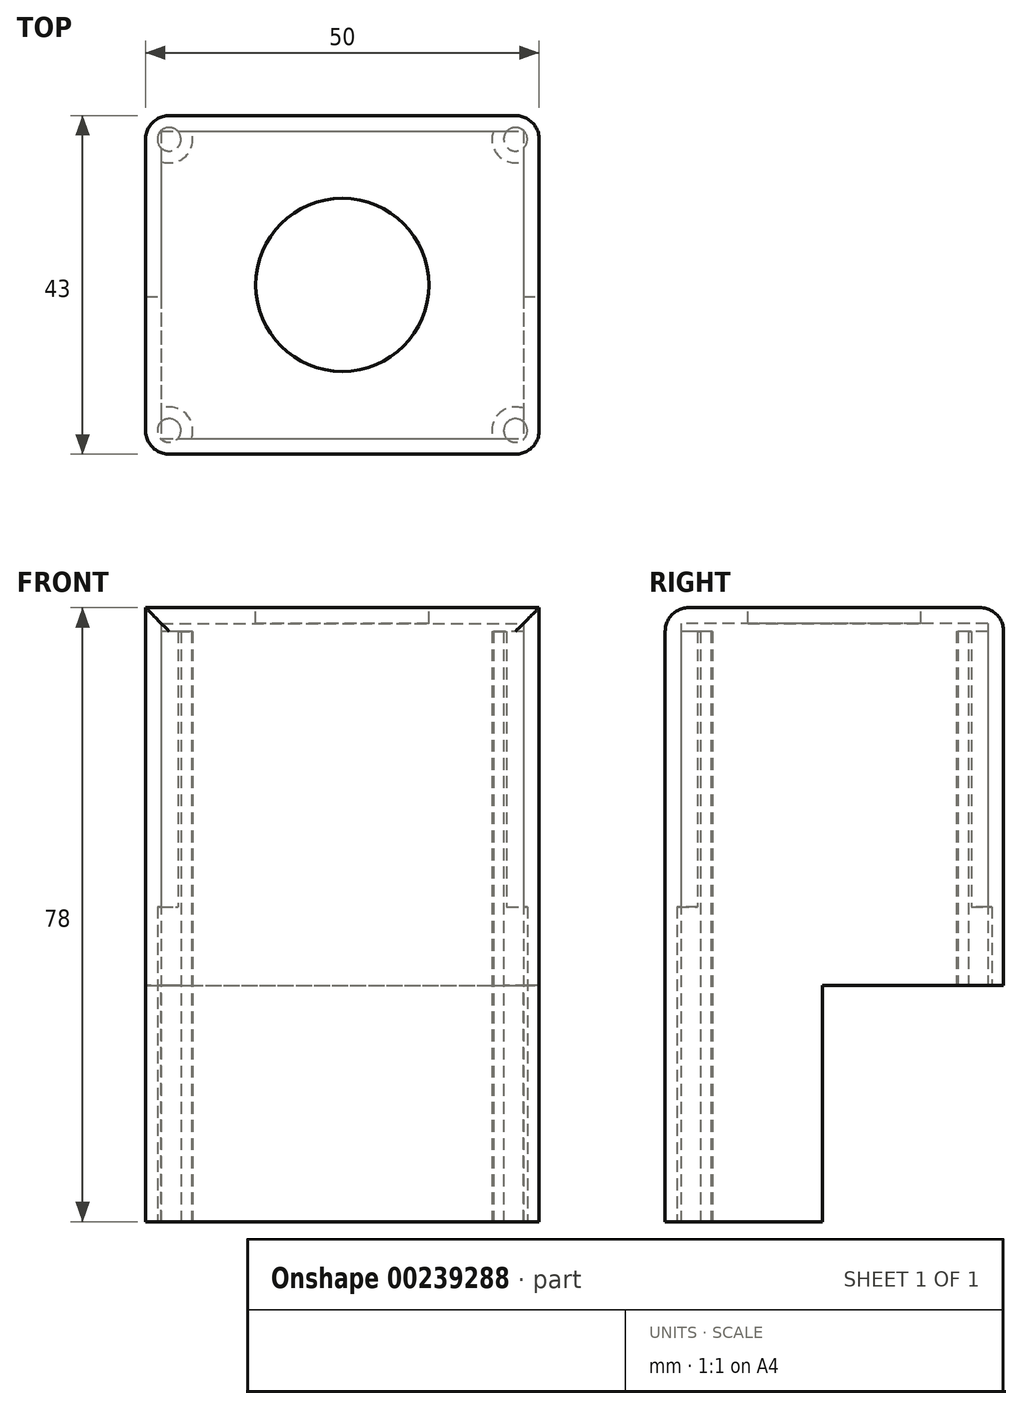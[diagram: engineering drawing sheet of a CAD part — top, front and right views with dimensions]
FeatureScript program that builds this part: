
annotation { "Feature Type Name" : "Feature", "Feature Type Description" : "" }
export const myFeature = defineFeature(function(context is Context, id is Id, definition is map)
    precondition{}
    {
        {
            var Q0;
            Q0=qCreatedBy(makeId("Top.planeOp"),FACE);
            var sketch = newSketch(context, id + "F0", { "sketchPlane" : qUnion([Q0])});
            skLineSegment(sketch, "E0.bottom", {"start": v(-34.03, 26.22) * mm, "end": v(15.97, 26.22) * mm});
            skLineSegment(sketch, "E0.top", {"start": v(-34.03, -16.78) * mm, "end": v(15.97, -16.78) * mm});
            skLineSegment(sketch, "E0.left", {"start": v(-34.03, 26.22) * mm, "end": v(-34.03, -16.78) * mm});
            skLineSegment(sketch, "E0.right", {"start": v(15.97, 26.22) * mm, "end": v(15.97, -16.78) * mm});
            skPoint(sketch, "E1", {"position": v(-31.03, -13.78) * mm});
            skPoint(sketch, "E2", {"position": v(-31.03, 23.22) * mm});
            skPoint(sketch, "E3", {"position": v(12.97, 23.22) * mm});
            skPoint(sketch, "E4", {"position": v(12.97, -13.78) * mm});
            skCircle(sketch, "E5", {"center": v(-31.03, 23.22) * mm, "radius": 1.5 * mm});
            skCircle(sketch, "E6", {"center": v(12.97, 23.22) * mm, "radius": 1.5 * mm});
            skCircle(sketch, "E7", {"center": v(-31.03, -13.78) * mm, "radius": 1.5 * mm});
            skCircle(sketch, "E8", {"center": v(12.97, -13.78) * mm, "radius": 1.5 * mm});
            skSolve(sketch);
        }
        {
            var Q0;
            Q0=makeQuery(id+"F0.imprint","IMPRINT",FACE,{"disambiguationData":[TD([[makeQuery(id+"F0.imprint","IMPRINT",EDGE,{"derivedFrom":sQuery(id+"F0.wireOp",EDGE,"E8")}),-1.0]])]});
            var Q1;
            Q1=makeQuery(id+"F0.imprint","IMPRINT",FACE,{"disambiguationData":[TD([[makeQuery(id+"F0.imprint","IMPRINT",EDGE,{"derivedFrom":sQuery(id+"F0.wireOp",EDGE,"E7")}),-1.0]])]});
            var Q2;
            Q2=makeQuery(id+"F0.imprint","IMPRINT",FACE,{"disambiguationData":[TD([[makeQuery(id+"F0.imprint","IMPRINT",EDGE,{"derivedFrom":sQuery(id+"F0.wireOp",EDGE,"E5")}),-1.0]])]});
            var Q3;
            Q3=makeQuery(id+"F0.imprint","IMPRINT",FACE,{"disambiguationData":[TD([[makeQuery(id+"F0.imprint","IMPRINT",EDGE,{"derivedFrom":sQuery(id+"F0.wireOp",EDGE,"E6")}),-1.0]])]});
            var Q4;
            {var subQ5=sQuery(id+"F0.wireOp",EDGE,"5a7f028d-dde4-426a-927e-fdb31705949f");var subQ13=sQuery(id+"F0.wireOp",EDGE,"E0.bottom");var subQ14=makeQuery(id+"F0.imprint","INTERSECT",VERTEX,{"derivedFrom":[subQ13,subQ5]});Q4=makeQuery(id+"F0.imprint","IMPRINT",FACE,{"disambiguationData":[TD([[makeQuery(id+"F0.imprint","IMPRINT",EDGE,{"disambiguationData":[TD([[subQ14,-1.0]])],"derivedFrom":subQ13}),-1.0]])]});}
            var Q5;
            Q5=makeQuery(id+"F0.imprint","IMPRINT",FACE,{"disambiguationData":[TD([[makeQuery(id+"F0.imprint","IMPRINT",EDGE,{"derivedFrom":sQuery(id+"F0.wireOp",EDGE,"E6")}),1.0]])]});
            var Q6;
            Q6=makeQuery(id+"F0.imprint","IMPRINT",FACE,{"disambiguationData":[TD([[makeQuery(id+"F0.imprint","IMPRINT",EDGE,{"derivedFrom":sQuery(id+"F0.wireOp",EDGE,"E8")}),1.0]])]});
            var Q7;
            Q7=makeQuery(id+"F0.imprint","IMPRINT",FACE,{"disambiguationData":[TD([[makeQuery(id+"F0.imprint","IMPRINT",EDGE,{"derivedFrom":sQuery(id+"F0.wireOp",EDGE,"E7")}),1.0]])]});
            var Q8;
            Q8=makeQuery(id+"F0.imprint","IMPRINT",FACE,{"disambiguationData":[TD([[makeQuery(id+"F0.imprint","IMPRINT",EDGE,{"derivedFrom":sQuery(id+"F0.wireOp",EDGE,"E5")}),1.0]])]});
            extrude(context, id + "F1", {"entities" : qUnion([Q0, Q1, Q2, Q3, Q4, Q5, Q6, Q7, Q8]), "depth" : 78 * mm});
        }
        {
            var Q0;
            Q0=makeQuery(id+"F1.opExtrude","CAP_FACE",FACE,{"disambiguationData":[OSD([sQuery(id+"F0.wireOp",EDGE,"E0.bottom"),sQuery(id+"F0.wireOp",EDGE,"E0.top"),sQuery(id+"F0.wireOp",EDGE,"E0.left"),sQuery(id+"F0.wireOp",EDGE,"E0.right")])],"isStart":false});
            var sketch = newSketch(context, id + "F2", { "sketchPlane" : qUnion([Q0])});
            skCircle(sketch, "E9", {"center": v(-9.03, 4.72) * mm, "radius": 11 * mm});
            skSolve(sketch);
        }
        {
            var Q0;
            Q0=makeQuery(id+"F1.opExtrude","CAP_FACE",FACE,{"disambiguationData":[OSD([sQuery(id+"F0.wireOp",EDGE,"E0.bottom"),sQuery(id+"F0.wireOp",EDGE,"E0.top"),sQuery(id+"F0.wireOp",EDGE,"E0.left"),sQuery(id+"F0.wireOp",EDGE,"E0.right")])],"isStart":true});
            shell(context, id + "F3", {"entities" : qUnion([Q0]), "thickness" : 2 * mm});
        }
        {
            var Q0;
            Q0=makeQuery(id+"F2.imprint","IMPRINT",FACE,{"disambiguationData":[TD([[makeQuery(id+"F2.imprint","IMPRINT",EDGE,{"derivedFrom":sQuery(id+"F2.wireOp",EDGE,"E9")}),1.0]])]});
            extrude(context, id + "F4", {"entities" : qUnion([Q0]), "operationType" : NewBodyOperationType.REMOVE, "oppositeDirection" : true, "depth" : 3.1 * mm});
        }
        {
            var Q0;
            Q0=makeQuery(id+"F1.opExtrude","SWEPT_EDGE",EDGE,{"disambiguationData":[OSD([sQuery(id+"F0.wireOp",EDGE,"E0.bottom"),sQuery(id+"F0.wireOp",EDGE,"E0.right")])]});
            var Q1;
            Q1=makeQuery(id+"F1.opExtrude","CAP_EDGE",EDGE,{"disambiguationData":[OSD([sQuery(id+"F0.wireOp",EDGE,"E0.bottom")])],"isStart":false});
            var Q2;
            Q2=makeQuery(id+"F1.opExtrude","SWEPT_EDGE",EDGE,{"disambiguationData":[OSD([sQuery(id+"F0.wireOp",EDGE,"E0.bottom"),sQuery(id+"F0.wireOp",EDGE,"E0.left")])]});
            var Q3;
            Q3=makeQuery(id+"F1.opExtrude","SWEPT_EDGE",EDGE,{"disambiguationData":[OSD([sQuery(id+"F0.wireOp",EDGE,"E0.top"),sQuery(id+"F0.wireOp",EDGE,"E0.right")])]});
            var Q4;
            Q4=makeQuery(id+"F1.opExtrude","CAP_EDGE",EDGE,{"disambiguationData":[OSD([sQuery(id+"F0.wireOp",EDGE,"E0.top")])],"isStart":false});
            var Q5;
            Q5=makeQuery(id+"F1.opExtrude","SWEPT_EDGE",EDGE,{"disambiguationData":[OSD([sQuery(id+"F0.wireOp",EDGE,"E0.top"),sQuery(id+"F0.wireOp",EDGE,"E0.left")])]});
            fillet(context, id + "F5", {"entities" : qUnion([Q0, Q1, Q2, Q3, Q4, Q5]), "radius" : 3 * mm, "tangentPropagation" : true, "allowEdgeOverflow" : false});
        }
        {
            var Q0;
            Q0=makeQuery(id+"F0.imprint","IMPRINT",FACE,{"disambiguationData":[TD([[makeQuery(id+"F0.imprint","IMPRINT",EDGE,{"derivedFrom":sQuery(id+"F0.wireOp",EDGE,"E0.bottom")}),-1.0]])]});
            var sketch = newSketch(context, id + "F6", { "sketchPlane" : qUnion([Q0])});
            skCircle(sketch, "E10", {"center": v(12.97, -13.78) * mm, "radius": 3 * mm});
            skCircle(sketch, "E11", {"center": v(12.97, 23.22) * mm, "radius": 3 * mm});
            skCircle(sketch, "E12", {"center": v(-31.03, -13.78) * mm, "radius": 3 * mm});
            skCircle(sketch, "E13", {"center": v(-31.03, 23.22) * mm, "radius": 3 * mm});
            skSolve(sketch);
        }
        {
            var Q0;
            Q0=makeQuery(id+"F6.imprint","IMPRINT",FACE,{"disambiguationData":[TD([[makeQuery(id+"F6.imprint","IMPRINT",EDGE,{"derivedFrom":makeQuery(id+"F0.imprint","IMPRINT",EDGE,{"derivedFrom":sQuery(id+"F0.wireOp",EDGE,"E8")})}),-1.0]])]});
            var Q1;
            Q1=makeQuery(id+"F6.imprint","IMPRINT",FACE,{"disambiguationData":[TD([[makeQuery(id+"F6.imprint","IMPRINT",EDGE,{"derivedFrom":makeQuery(id+"F0.imprint","IMPRINT",EDGE,{"derivedFrom":sQuery(id+"F0.wireOp",EDGE,"E6")})}),-1.0]])]});
            var Q2;
            Q2=makeQuery(id+"F6.imprint","IMPRINT",FACE,{"disambiguationData":[TD([[makeQuery(id+"F6.imprint","IMPRINT",EDGE,{"derivedFrom":makeQuery(id+"F0.imprint","IMPRINT",EDGE,{"derivedFrom":sQuery(id+"F0.wireOp",EDGE,"E7")})}),-1.0]])]});
            var Q3;
            Q3=makeQuery(id+"F6.imprint","IMPRINT",FACE,{"disambiguationData":[TD([[makeQuery(id+"F6.imprint","IMPRINT",EDGE,{"derivedFrom":makeQuery(id+"F0.imprint","IMPRINT",EDGE,{"derivedFrom":sQuery(id+"F0.wireOp",EDGE,"E5")})}),-1.0]])]});
            extrude(context, id + "F7", {"entities" : qUnion([Q0, Q1, Q2, Q3]), "operationType" : NewBodyOperationType.ADD, "depth" : 75 * mm});
        }
        {
            var Q0;
            Q0=makeQuery(id+"F0.imprint","IMPRINT",FACE,{"disambiguationData":[TD([[makeQuery(id+"F0.imprint","IMPRINT",EDGE,{"derivedFrom":sQuery(id+"F0.wireOp",EDGE,"E5")}),1.0]])]});
            var Q1;
            Q1=makeQuery(id+"F0.imprint","IMPRINT",FACE,{"disambiguationData":[TD([[makeQuery(id+"F0.imprint","IMPRINT",EDGE,{"derivedFrom":sQuery(id+"F0.wireOp",EDGE,"E6")}),1.0]])]});
            var Q2;
            Q2=makeQuery(id+"F0.imprint","IMPRINT",FACE,{"disambiguationData":[TD([[makeQuery(id+"F0.imprint","IMPRINT",EDGE,{"derivedFrom":sQuery(id+"F0.wireOp",EDGE,"E7")}),1.0]])]});
            var Q3;
            Q3=makeQuery(id+"F0.imprint","IMPRINT",FACE,{"disambiguationData":[TD([[makeQuery(id+"F0.imprint","IMPRINT",EDGE,{"derivedFrom":sQuery(id+"F0.wireOp",EDGE,"E8")}),1.0]])]});
            extrude(context, id + "F8", {"entities" : qUnion([Q0, Q1, Q2, Q3]), "operationType" : NewBodyOperationType.REMOVE, "depth" : 40 * mm});
        }
        {
            var Q0;
            Q0=qCreatedBy(makeId("Top.planeOp"),FACE);
            var sketch = newSketch(context, id + "F9", { "sketchPlane" : qUnion([Q0])});
            skLineSegment(sketch, "E14.bottom", {"start": v(-34.03, 26.22) * mm, "end": v(15.97, 26.22) * mm});
            skLineSegment(sketch, "E14.top", {"start": v(-34.03, 3.22) * mm, "end": v(15.97, 3.22) * mm});
            skLineSegment(sketch, "E14.left", {"start": v(-34.03, 26.22) * mm, "end": v(-34.03, 3.22) * mm});
            skLineSegment(sketch, "E14.right", {"start": v(15.97, 26.22) * mm, "end": v(15.97, 3.22) * mm});
            skSolve(sketch);
        }
        {
            var Q0;
            Q0 = qSketchRegion(id + "F9", true);
            extrude(context, id + "F10", {"entities" : qUnion([Q0]), "operationType" : NewBodyOperationType.REMOVE, "depth" : 30 * mm});
        }
    });
